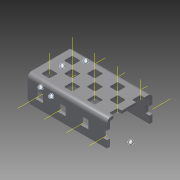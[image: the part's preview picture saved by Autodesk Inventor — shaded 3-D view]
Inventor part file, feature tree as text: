
AUTODESK INVENTOR PART (.ipt)
format: ipt  version: 2015 (Build 190159000, 159)  size: 1,927,680 bytes
history: native  units: in
note: dims shown in document units (in); Inventor stores cm internally (conversion verified against a paired STEP export)
features: other x26, pattern_linear x3, sheet_metal_op x1, extrude x1, imported_body x1, sketch x1
ambient origin geometry x8: Origin, YZ Plane, XZ Plane, XY Plane, X Axis, Y Axis, Z Axis, Center Point
bodies: Body1 (feature_tree)
feature tree (33):
  sheet_metal_op  "Fold1"
  other  "C-Channel"
  extrude  "length cut"  Depth=0.5in
  other  "top axis"
  other  "inner axis"
  other  "front axis"
  other  "back axis"
  pattern_linear  "top axes"  Spacing1=0.5in  [1 undecoded]
  pattern_linear  "inner axes"  Spacing1=0.5in  [1 undecoded]
  pattern_linear  "horiz axes"  Spacing1=-1.75in  [1 undecoded]
  other  "right plane"
  imported_body  "Base1"
  sketch  "Sketch1"  dims[d1=0.0in d4=0.5in d5=0.7874in d7=0.5in d10=0.5in d13=0.5in d14=-1.75in d15=0.0in d16=0.0in d17=0.0in d18=0.0in d19=0.0in]
  other  "Work Point1"
  other  "Work Point2"
  other  "Work Point3"
  other  "Work Point4"
  other  "Work Axis5"
  other  "Work Axis6"
  other  "Work Axis7"
  other  "Work Axis11"
  other  "Work Axis12"
  other  "Work Axis13"
  other  "Work Axis14"
  other  "Work Axis18"
  other  "Work Axis19"
  other  "Work Axis23"
  other  "Work Axis24"
  other  "Work Axis25"
  other  "Work Axis30"
  other  "Work Axis31"
  other  "Work Axis32"
  other  "left plane"
note: 3 required parameter values undecoded (feature->parameter linkage not recoverable at this tier; creation-order binding heuristic only, values carry confidence <= 0.55)
